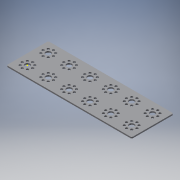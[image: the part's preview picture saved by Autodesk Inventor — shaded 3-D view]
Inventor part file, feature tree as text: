
AUTODESK INVENTOR PART (.ipt)
format: ipt  version: 2019 (Build 230136000, 136)  size: 272,896 bytes
history: native  units: in
note: dims shown in document units (in); Inventor stores cm internally (conversion verified against a paired STEP export)
features: other x1, imported_body x1, sketch x1
ambient origin geometry x8: Origin, YZ Plane, XZ Plane, XY Plane, X Axis, Y Axis, Z Axis, Center Point
bodies: Body1 (feature_tree)
feature tree (3):
  other  "PLATE_64MM_X_192MM_2011"
  imported_body  "Base1"
  sketch  "Sketch1"
